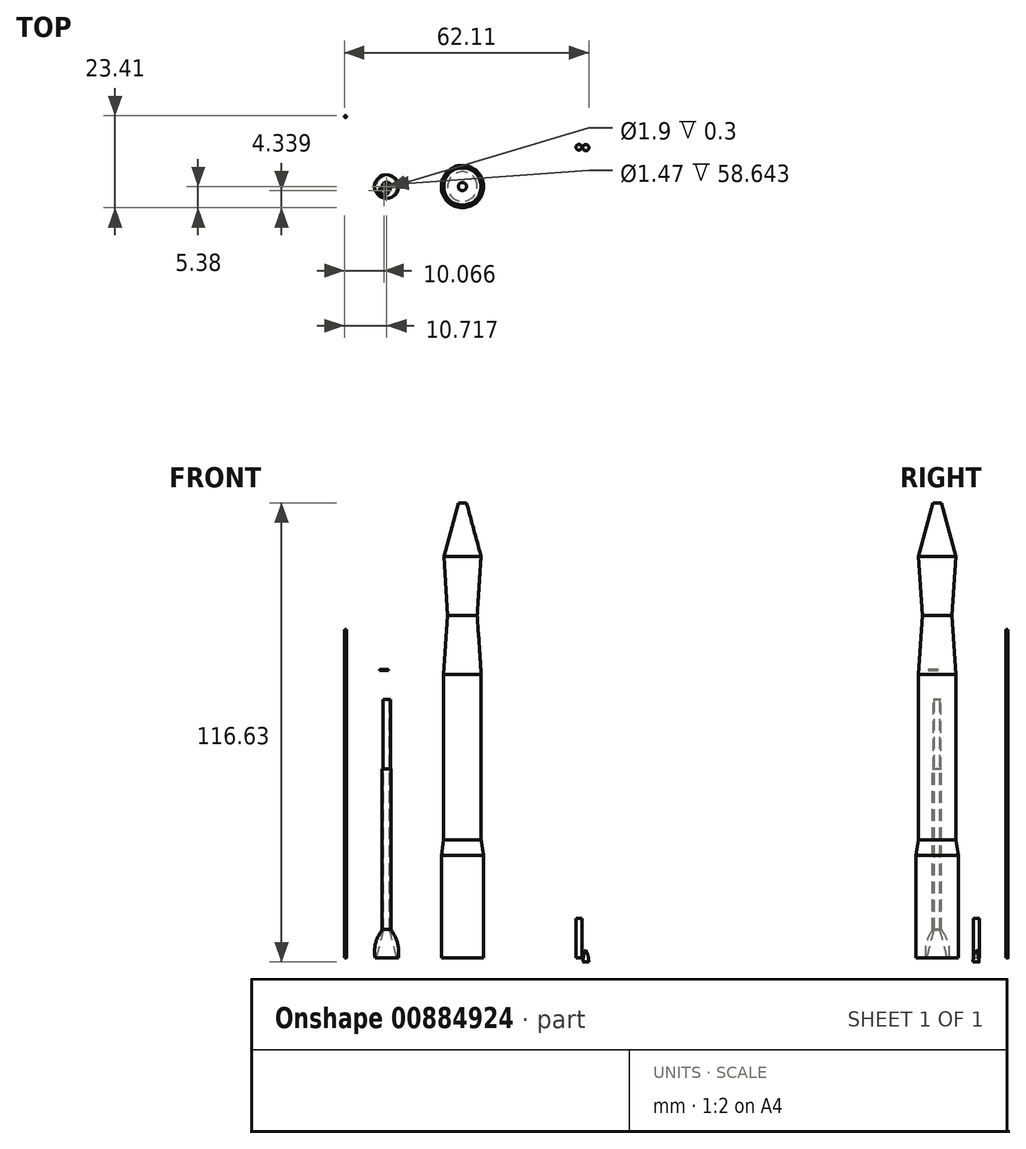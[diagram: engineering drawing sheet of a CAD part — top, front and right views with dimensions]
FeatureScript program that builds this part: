
annotation { "Feature Type Name" : "Feature", "Feature Type Description" : "" }
export const myFeature = defineFeature(function(context is Context, id is Id, definition is map)
    precondition{}
    {
        {
            var Q0;
            Q0=qCreatedBy(makeId("Top.planeOp"),FACE);
            var sketch = newSketch(context, id + "F0", { "sketchPlane" : qUnion([Q0])});
            skCircle(sketch, "E0", {"center": v(0, 0) * mm, "radius": 5.38 * mm});
            skSolve(sketch);
        }
        {
            var Q0;
            Q0=makeQuery(id+"F0.imprint","IMPRINT",FACE,{"disambiguationData":[TD([[makeQuery(id+"F0.imprint","IMPRINT",EDGE,{"derivedFrom":sQuery(id+"F0.wireOp",EDGE,"E0")}),1.0]])]});
            cPlane(context, id + "F1", {"entities" : qUnion([Q0]), "cplaneType" : CPlaneType.OFFSET, "offset" : 26 * mm, "width" : 150 * mm, "height" : 150 * mm});
        }
        {
            var Q0;
            Q0=qCreatedBy(id+"F1.planeOp",FACE);
            var sketch = newSketch(context, id + "F2", { "sketchPlane" : qUnion([Q0])});
            skCircle(sketch, "E1", {"center": v(0, 0) * mm, "radius": 5.38 * mm});
            skSolve(sketch);
        }
        {
            var Q0;
            Q0=makeQuery(id+"F2.imprint","IMPRINT",FACE,{"disambiguationData":[TD([[makeQuery(id+"F2.imprint","IMPRINT",EDGE,{"derivedFrom":sQuery(id+"F2.wireOp",EDGE,"E1")}),1.0]])]});
            cPlane(context, id + "F3", {"entities" : qUnion([Q0]), "cplaneType" : CPlaneType.OFFSET, "offset" : 4 * mm, "width" : 150 * mm, "height" : 150 * mm});
        }
        {
            var Q0;
            Q0=qCreatedBy(id+"F3.planeOp",FACE);
            var sketch = newSketch(context, id + "F4", { "sketchPlane" : qUnion([Q0])});
            skCircle(sketch, "E2", {"center": v(0, 0) * mm, "radius": 4.75 * mm});
            skSolve(sketch);
        }
        {
            var Q0;
            Q0=makeQuery(id+"F4.imprint","IMPRINT",FACE,{"disambiguationData":[TD([[makeQuery(id+"F4.imprint","IMPRINT",EDGE,{"derivedFrom":sQuery(id+"F4.wireOp",EDGE,"E2")}),1.0]])]});
            cPlane(context, id + "F5", {"entities" : qUnion([Q0]), "cplaneType" : CPlaneType.OFFSET, "offset" : 42 * mm, "width" : 150 * mm, "height" : 150 * mm});
        }
        {
            var Q0;
            Q0=qCreatedBy(id+"F5.planeOp",FACE);
            var sketch = newSketch(context, id + "F6", { "sketchPlane" : qUnion([Q0])});
            skCircle(sketch, "E3", {"center": v(0, 0) * mm, "radius": 4.78 * mm});
            skSolve(sketch);
        }
        {
            var Q0;
            Q0=makeQuery(id+"F4.imprint","IMPRINT",FACE,{"disambiguationData":[TD([[makeQuery(id+"F4.imprint","IMPRINT",EDGE,{"derivedFrom":sQuery(id+"F4.wireOp",EDGE,"E2")}),1.0]])]});
            extrude(context, id + "F7", {"entities" : qUnion([Q0]), "depth" : 42 * mm, "offsetDistance" : 25 * mm});
        }
        {
            var Q0;
            Q0=makeQuery(id+"F0.imprint","IMPRINT",FACE,{"disambiguationData":[TD([[makeQuery(id+"F0.imprint","IMPRINT",EDGE,{"derivedFrom":sQuery(id+"F0.wireOp",EDGE,"E0")}),1.0]])]});
            extrude(context, id + "F8", {"entities" : qUnion([Q0]), "depth" : 26 * mm, "offsetDistance" : 25 * mm});
        }
        {
            var Q0;
            Q0=makeQuery(id+"F2.imprint","IMPRINT",FACE,{"disambiguationData":[TD([[makeQuery(id+"F2.imprint","IMPRINT",EDGE,{"derivedFrom":sQuery(id+"F2.wireOp",EDGE,"E1")}),1.0]])]});
            var Q1;
            Q1=makeQuery(id+"F7.opExtrude","CAP_FACE",FACE,{"disambiguationData":[OSD([sQuery(id+"F4.wireOp",EDGE,"E2")])],"isStart":true});
            loft(context, id + "F9", {"sheetProfilesArray" : [{ "sheetProfileEntities" : qUnion([Q0]) }, { "sheetProfileEntities" : qUnion([Q1]) }]});
        }
        {
            var Q0;
            Q0=makeQuery(id+"F6.imprint","IMPRINT",FACE,{"disambiguationData":[TD([[makeQuery(id+"F6.imprint","IMPRINT",EDGE,{"derivedFrom":sQuery(id+"F6.wireOp",EDGE,"E3")}),1.0]])]});
            cPlane(context, id + "F10", {"entities" : qUnion([Q0]), "cplaneType" : CPlaneType.OFFSET, "offset" : 15 * mm, "width" : 150 * mm, "height" : 150 * mm});
        }
        {
            var Q0;
            Q0=qCreatedBy(id+"F10.planeOp",FACE);
            var sketch = newSketch(context, id + "F11", { "sketchPlane" : qUnion([Q0])});
            skCircle(sketch, "E4", {"center": v(0, 0) * mm, "radius": 3.75 * mm});
            skSolve(sketch);
        }
        {
            var Q1;
            Q1=makeQuery(id+"F6.imprint","IMPRINT",FACE,{"disambiguationData":[TD([[makeQuery(id+"F6.imprint","IMPRINT",EDGE,{"derivedFrom":sQuery(id+"F6.wireOp",EDGE,"E3")}),1.0]])]});
            var Q2;
            Q2=makeQuery(id+"F11.imprint","IMPRINT",FACE,{"disambiguationData":[TD([[makeQuery(id+"F11.imprint","IMPRINT",EDGE,{"derivedFrom":sQuery(id+"F11.wireOp",EDGE,"E4")}),1.0]])]});
            loft(context, id + "F12", {"operationType" : NewBodyOperationType.ADD, "sheetProfilesArray" : [{ "sheetProfileEntities" : qUnion([Q1]) }, { "sheetProfileEntities" : qUnion([Q2]) }]});
        }
        {
            var Q0;
            Q0=qCreatedBy(id+"F10.planeOp",FACE);
            cPlane(context, id + "F13", {"entities" : qUnion([Q0]), "cplaneType" : CPlaneType.OFFSET, "offset" : 15 * mm, "width" : 150 * mm, "height" : 150 * mm});
        }
        {
            var Q0;
            Q0=qCreatedBy(id+"F13.planeOp",FACE);
            var sketch = newSketch(context, id + "F14", { "sketchPlane" : qUnion([Q0])});
            skCircle(sketch, "E5", {"center": v(0, 0) * mm, "radius": 4.74 * mm});
            skSolve(sketch);
        }
        {
            var Q1;
            Q1=makeQuery(id+"F12.opLoft","CAP_FACE",FACE,{"disambiguationData":[OSD([makeQuery(id+"F11.imprint","IMPRINT",FACE,{"disambiguationData":[TD([[makeQuery(id+"F11.imprint","IMPRINT",EDGE,{"derivedFrom":sQuery(id+"F11.wireOp",EDGE,"E4")}),1.0]])]})])],"isStart":true});
            var Q2;
            Q2=makeQuery(id+"F14.imprint","IMPRINT",FACE,{"disambiguationData":[TD([[makeQuery(id+"F14.imprint","IMPRINT",EDGE,{"derivedFrom":sQuery(id+"F14.wireOp",EDGE,"E5")}),1.0]])]});
            loft(context, id + "F15", {"operationType" : NewBodyOperationType.ADD, "sheetProfilesArray" : [{ "sheetProfileEntities" : qUnion([Q1]) }, { "sheetProfileEntities" : qUnion([Q2]) }]});
        }
        {
            var Q0;
            Q0=qCreatedBy(makeId("Top.planeOp"),FACE);
            var sketch = newSketch(context, id + "F16", { "sketchPlane" : qUnion([Q0])});
            skCircle(sketch, "E6", {"center": v(-21.4, 0) * mm, "radius": 3.3 * mm});
            skSolve(sketch);
        }
        {
            var Q0;
            Q0=makeQuery(id+"F16.imprint","IMPRINT",FACE,{"disambiguationData":[TD([[makeQuery(id+"F16.imprint","IMPRINT",EDGE,{"derivedFrom":sQuery(id+"F16.wireOp",EDGE,"E6")}),1.0]])]});
            cPlane(context, id + "F17", {"entities" : qUnion([Q0]), "cplaneType" : CPlaneType.OFFSET, "offset" : 4 * mm, "width" : 150 * mm, "height" : 150 * mm});
        }
        {
            var Q0;
            Q0=makeQuery(id+"F16.imprint","IMPRINT",FACE,{"disambiguationData":[TD([[makeQuery(id+"F16.imprint","IMPRINT",EDGE,{"derivedFrom":sQuery(id+"F16.wireOp",EDGE,"E6")}),1.0]])]});
            cPlane(context, id + "F18", {"entities" : qUnion([Q0]), "cplaneType" : CPlaneType.OFFSET, "offset" : 8 * mm, "width" : 150 * mm, "height" : 150 * mm});
        }
        {
            var Q0;
            Q0=qCreatedBy(id+"F17.planeOp",FACE);
            var sketch = newSketch(context, id + "F19", { "sketchPlane" : qUnion([Q0])});
            skCircle(sketch, "E7", {"center": v(-21.4, 0) * mm, "radius": 3.15 * mm});
            skSolve(sketch);
        }
        {
            var Q0;
            Q0=qCreatedBy(id+"F18.planeOp",FACE);
            var sketch = newSketch(context, id + "F20", { "sketchPlane" : qUnion([Q0])});
            skCircle(sketch, "E8", {"center": v(-21.4, 0) * mm, "radius": 1.25 * mm});
            skSolve(sketch);
        }
        {
            var Q0;
            Q0=makeQuery(id+"F20.imprint","IMPRINT",FACE,{"disambiguationData":[TD([[makeQuery(id+"F20.imprint","IMPRINT",EDGE,{"derivedFrom":sQuery(id+"F20.wireOp",EDGE,"E8")}),1.0]])]});
            cPlane(context, id + "F21", {"entities" : qUnion([Q0]), "cplaneType" : CPlaneType.OFFSET, "offset" : 65 * mm, "width" : 150 * mm, "height" : 150 * mm});
        }
        {
            var Q0;
            Q0=qCreatedBy(id+"F21.planeOp",FACE);
            var sketch = newSketch(context, id + "F22", { "sketchPlane" : qUnion([Q0])});
            skCircle(sketch, "E9", {"center": v(-21.4, 0) * mm, "radius": 1.26 * mm});
            skSolve(sketch);
        }
        {
            var Q0;
            Q0=makeQuery(id+"F16.imprint","IMPRINT",FACE,{"disambiguationData":[TD([[makeQuery(id+"F16.imprint","IMPRINT",EDGE,{"derivedFrom":sQuery(id+"F16.wireOp",EDGE,"E6")}),1.0]])]});
            var Q1;
            Q1=makeQuery(id+"F19.imprint","IMPRINT",FACE,{"disambiguationData":[TD([[makeQuery(id+"F19.imprint","IMPRINT",EDGE,{"derivedFrom":sQuery(id+"F19.wireOp",EDGE,"E7")}),1.0]])]});
            var Q2;
            Q2=makeQuery(id+"F20.imprint","IMPRINT",FACE,{"disambiguationData":[TD([[makeQuery(id+"F20.imprint","IMPRINT",EDGE,{"derivedFrom":sQuery(id+"F20.wireOp",EDGE,"E8")}),1.0]])]});
            loft(context, id + "F23", {"sheetProfilesArray" : [{ "sheetProfileEntities" : qUnion([Q0]) }, { "sheetProfileEntities" : qUnion([Q1]) }, { "sheetProfileEntities" : qUnion([Q2]) }]});
        }
        {
            var Q0;
            Q0=makeQuery(id+"F22.imprint","IMPRINT",FACE,{"disambiguationData":[TD([[makeQuery(id+"F22.imprint","IMPRINT",EDGE,{"derivedFrom":sQuery(id+"F22.wireOp",EDGE,"E9")}),1.0]])]});
            var Q1;
            Q1=makeQuery(id+"F23.opLoft","CAP_FACE",FACE,{"disambiguationData":[OSD([makeQuery(id+"F20.imprint","IMPRINT",FACE,{"disambiguationData":[TD([[makeQuery(id+"F20.imprint","IMPRINT",EDGE,{"derivedFrom":sQuery(id+"F20.wireOp",EDGE,"E8")}),1.0]])]})])],"isStart":true});
            extrude(context, id + "F24", {"entities" : qUnion([Q0]), "operationType" : NewBodyOperationType.ADD, "endBound" : BoundingType.UP_TO_SURFACE, "oppositeDirection" : true, "depth" : 25 * mm, "endBoundEntityFace" : qUnion([Q1]), "offsetDistance" : 25 * mm});
        }
        {
            var Q0;
            Q0=qCreatedBy(id+"F21.planeOp",FACE);
            var sketch = newSketch(context, id + "F25", { "sketchPlane" : qUnion([Q0])});
            skCircle(sketch, "E10", {"center": v(-21.4, 0) * mm, "radius": 0.82 * mm});
            skSolve(sketch);
        }
        {
            var Q0;
            Q0 = qSketchRegion(id + "F25", true);
            extrude(context, id + "F26", {"entities" : qUnion([Q0]), "operationType" : NewBodyOperationType.REMOVE, "oppositeDirection" : true, "depth" : 1000 * mm, "offsetDistance" : 25 * mm});
        }
        {
            var Q0;
            Q0=qCreatedBy(makeId("Top.planeOp"),FACE);
            var sketch = newSketch(context, id + "F27", { "sketchPlane" : qUnion([Q0])});
            skCircle(sketch, "E11", {"center": v(-21.4, 0) * mm, "radius": 2.87 * mm});
            skSolve(sketch);
        }
        {
            var Q0;
            Q0=qCreatedBy(id+"F18.planeOp",FACE);
            var sketch = newSketch(context, id + "F28", { "sketchPlane" : qUnion([Q0])});
            skCircle(sketch, "E12", {"center": v(-21.38, 0) * mm, "radius": 0.8 * mm});
            skSolve(sketch);
        }
        {
            var Q1;
            Q1 = qSketchRegion(id + "F27", true);
            var Q2;
            Q2 = qSketchRegion(id + "F28", true);
            loft(context, id + "F29", {"operationType" : NewBodyOperationType.REMOVE, "sheetProfilesArray" : [{ "sheetProfileEntities" : qUnion([Q1]) }, { "sheetProfileEntities" : qUnion([Q2]) }]});
        }
        {
            var Q0;
            Q0=makeQuery(id+"F23.opLoft","SWEPT_BODY",BODY,{"disambiguationData":[OSD([makeQuery(id+"F16.imprint","IMPRINT",FACE,{"disambiguationData":[TD([[makeQuery(id+"F16.imprint","IMPRINT",EDGE,{"derivedFrom":sQuery(id+"F16.wireOp",EDGE,"E6")}),1.0]])]}),sQuery(id+"F19.wireOp",EDGE,"E7"),makeQuery(id+"F20.imprint","IMPRINT",FACE,{"disambiguationData":[TD([[makeQuery(id+"F20.imprint","IMPRINT",EDGE,{"derivedFrom":sQuery(id+"F20.wireOp",EDGE,"E8")}),1.0]])]})])]});
            var Q1;
            Q1=qCreatedBy(makeId("Origin.pointOp"),VERTEX);
            transform(context, id + "F30", {"entities" : qUnion([Q0]), "transformType" : TransformType.SCALE_UNIFORMLY, "scale" : .9, "scalePoint" : qUnion([Q1]), "makeCopy" : false});
        }
        {
            var Q0;
            Q0=qCreatedBy(id+"F21.planeOp",FACE);
            var sketch = newSketch(context, id + "F31", { "sketchPlane" : qUnion([Q0])});
            skCircle(sketch, "E13", {"center": v(-19.27, 0.01) * mm, "radius": 1.19 * mm});
            skCircle(sketch, "E14", {"center": v(-19.27, 0.01) * mm, "radius": 0.95 * mm});
            skSolve(sketch);
        }
        {
            var Q0;
            Q0=makeQuery(id+"F31.imprint","IMPRINT",FACE,{"disambiguationData":[TD([[makeQuery(id+"F31.imprint","IMPRINT",EDGE,{"derivedFrom":sQuery(id+"F31.wireOp",EDGE,"E13")}),1.0]])]});
            extrude(context, id + "F32", {"entities" : qUnion([Q0]), "operationType" : NewBodyOperationType.REMOVE, "oppositeDirection" : true, "depth" : 25 * mm, "offsetDistance" : 25 * mm});
        }
        {
            var Q0;
            Q0=qCreatedBy(id+"F21.planeOp",FACE);
            var sketch = newSketch(context, id + "F33", { "sketchPlane" : qUnion([Q0])});
            skCircle(sketch, "E15", {"center": v(-19.91, -1.04) * mm, "radius": 1.19 * mm});
            skCircle(sketch, "E16", {"center": v(-19.91, -1.04) * mm, "radius": 0.95 * mm});
            skSolve(sketch);
        }
        {
            var Q0;
            Q0=makeQuery(id+"F33.imprint","IMPRINT",FACE,{"disambiguationData":[TD([[makeQuery(id+"F33.imprint","IMPRINT",EDGE,{"derivedFrom":sQuery(id+"F33.wireOp",EDGE,"E15")}),1.0]])]});
            extrude(context, id + "F34", {"entities" : qUnion([Q0]), "depth" : .3 * mm, "offsetDistance" : 25 * mm});
        }
        {
            var Q0;
            Q0=qCreatedBy(makeId("Top.planeOp"),FACE);
            var sketch = newSketch(context, id + "F35", { "sketchPlane" : qUnion([Q0])});
            skCircle(sketch, "E17", {"center": v(-29.73, 17.78) * mm, "radius": 0.25 * mm});
            skSolve(sketch);
        }
        {
            var Q0;
            Q0=makeQuery(id+"F35.imprint","IMPRINT",FACE,{"disambiguationData":[TD([[makeQuery(id+"F35.imprint","IMPRINT",EDGE,{"derivedFrom":sQuery(id+"F35.wireOp",EDGE,"E17")}),1.0]])]});
            extrude(context, id + "F36", {"entities" : qUnion([Q0]), "depth" : 83.4 * mm, "offsetDistance" : 25 * mm});
        }
        {
            var Q0;
            Q0=makeQuery(id+"F15.opLoft","CAP_FACE",FACE,{"disambiguationData":[OSD([makeQuery(id+"F14.imprint","IMPRINT",FACE,{"disambiguationData":[TD([[makeQuery(id+"F14.imprint","IMPRINT",EDGE,{"derivedFrom":sQuery(id+"F14.wireOp",EDGE,"E5")}),1.0]])]})])],"isStart":true});
            cPlane(context, id + "F37", {"entities" : qUnion([Q0]), "cplaneType" : CPlaneType.OFFSET, "offset" : 13.6 * mm, "width" : 150 * mm, "height" : 150 * mm});
        }
        {
            var Q0;
            Q0=qCreatedBy(id+"F37.planeOp",FACE);
            var sketch = newSketch(context, id + "F38", { "sketchPlane" : qUnion([Q0])});
            skCircle(sketch, "E18", {"center": v(0, 0) * mm, "radius": 1.04 * mm});
            skSolve(sketch);
        }
        {
            var Q1;
            Q1=makeQuery(id+"F15.opLoft","CAP_FACE",FACE,{"disambiguationData":[OSD([makeQuery(id+"F14.imprint","IMPRINT",FACE,{"disambiguationData":[TD([[makeQuery(id+"F14.imprint","IMPRINT",EDGE,{"derivedFrom":sQuery(id+"F14.wireOp",EDGE,"E5")}),1.0]])]})])],"isStart":true});
            var Q2;
            Q2=makeQuery(id+"F38.imprint","IMPRINT",FACE,{"disambiguationData":[TD([[makeQuery(id+"F38.imprint","IMPRINT",EDGE,{"derivedFrom":sQuery(id+"F38.wireOp",EDGE,"E18")}),1.0]])]});
            loft(context, id + "F39", {"operationType" : NewBodyOperationType.ADD, "sheetProfilesArray" : [{ "sheetProfileEntities" : qUnion([Q1]) }, { "sheetProfileEntities" : qUnion([Q2]) }]});
        }
        {
            var Q0;
            Q0=qCreatedBy(makeId("Top.planeOp"),FACE);
            var sketch = newSketch(context, id + "F40", { "sketchPlane" : qUnion([Q0])});
            skCircle(sketch, "E19", {"center": v(29.59, 9.99) * mm, "radius": 0.74 * mm});
            skSolve(sketch);
        }
        {
            var Q0;
            Q0=makeQuery(id+"F40.imprint","IMPRINT",FACE,{"disambiguationData":[TD([[makeQuery(id+"F40.imprint","IMPRINT",EDGE,{"derivedFrom":sQuery(id+"F40.wireOp",EDGE,"E19")}),1.0]])]});
            var Q1;
            Q1=sQuery(id+"F40.wireOp",EDGE,"E19");
            extrude(context, id + "F41", {"entities" : qUnion([Q0]), "surfaceEntities" : qUnion([Q1]), "depth" : 10 * mm, "offsetDistance" : 25 * mm});
        }
        {
            var Q0;
            Q0=qCreatedBy(makeId("Top.planeOp"),FACE);
            var sketch = newSketch(context, id + "F42", { "sketchPlane" : qUnion([Q0])});
            skCircle(sketch, "E20", {"center": v(31.34, 9.88) * mm, "radius": 0.53 * mm});
            skSolve(sketch);
        }
        {
            var Q0;
            Q0=makeQuery(id+"F42.imprint","IMPRINT",FACE,{"disambiguationData":[TD([[makeQuery(id+"F42.imprint","IMPRINT",EDGE,{"derivedFrom":sQuery(id+"F42.wireOp",EDGE,"E20")}),1.0]])]});
            cPlane(context, id + "F43", {"entities" : qUnion([Q0]), "cplaneType" : CPlaneType.OFFSET, "offset" : 1.45 * mm, "width" : 150 * mm, "height" : 150 * mm});
        }
        {
            var Q0;
            Q0=qCreatedBy(id+"F43.planeOp",FACE);
            var sketch = newSketch(context, id + "F44", { "sketchPlane" : qUnion([Q0])});
            skCircle(sketch, "E21", {"center": v(31.34, 9.88) * mm, "radius": 0.26 * mm});
            skSolve(sketch);
        }
        {
            var Q0;
            Q0=makeQuery(id+"F44.imprint","IMPRINT",FACE,{"disambiguationData":[TD([[makeQuery(id+"F44.imprint","IMPRINT",EDGE,{"derivedFrom":sQuery(id+"F44.wireOp",EDGE,"E21")}),1.0]])]});
            cPlane(context, id + "F45", {"entities" : qUnion([Q0]), "cplaneType" : CPlaneType.OFFSET, "offset" : 0.6 * mm, "width" : 150 * mm, "height" : 150 * mm});
        }
        {
            var Q0;
            Q0=qCreatedBy(id+"F45.planeOp",FACE);
            var sketch = newSketch(context, id + "F46", { "sketchPlane" : qUnion([Q0])});
            skCircle(sketch, "E22", {"center": v(31.34, 9.88) * mm, "radius": 0.08 * mm});
            skSolve(sketch);
        }
        {
            var Q0;
            Q0=makeQuery(id+"F42.imprint","IMPRINT",FACE,{"disambiguationData":[TD([[makeQuery(id+"F42.imprint","IMPRINT",EDGE,{"derivedFrom":sQuery(id+"F42.wireOp",EDGE,"E20")}),1.0]])]});
            var Q1;
            Q1=makeQuery(id+"F44.imprint","IMPRINT",FACE,{"disambiguationData":[TD([[makeQuery(id+"F44.imprint","IMPRINT",EDGE,{"derivedFrom":sQuery(id+"F44.wireOp",EDGE,"E21")}),1.0]])]});
            var Q2;
            Q2=sQuery(id+"F46.wireOp",VERTEX,"E22.center");
            loft(context, id + "F47", {"sheetProfilesArray" : [{ "sheetProfileEntities" : qUnion([Q0]) }, { "sheetProfileEntities" : qUnion([Q1]) }, { "sheetProfileEntities" : qUnion([Q2]) }]});
        }
        {
            var Q0;
            Q0=makeQuery(id+"F47.opLoft","SWEPT_BODY",BODY,{"disambiguationData":[OSD([makeQuery(id+"F42.imprint","IMPRINT",FACE,{"disambiguationData":[TD([[makeQuery(id+"F42.imprint","IMPRINT",EDGE,{"derivedFrom":sQuery(id+"F42.wireOp",EDGE,"E20")}),1.0]])]}),sQuery(id+"F44.wireOp",EDGE,"E21"),sQuery(id+"F46.wireOp",VERTEX,"E22.center")])]});
            var Q1;
            Q1=qCreatedBy(id+"F47.opLoft",VERTEX);
            transform(context, id + "F48", {"entities" : qUnion([Q0]), "transformType" : TransformType.SCALE_UNIFORMLY, "scale" : 1.5, "scalePoint" : qUnion([Q1]), "makeCopy" : false});
        }
    });
